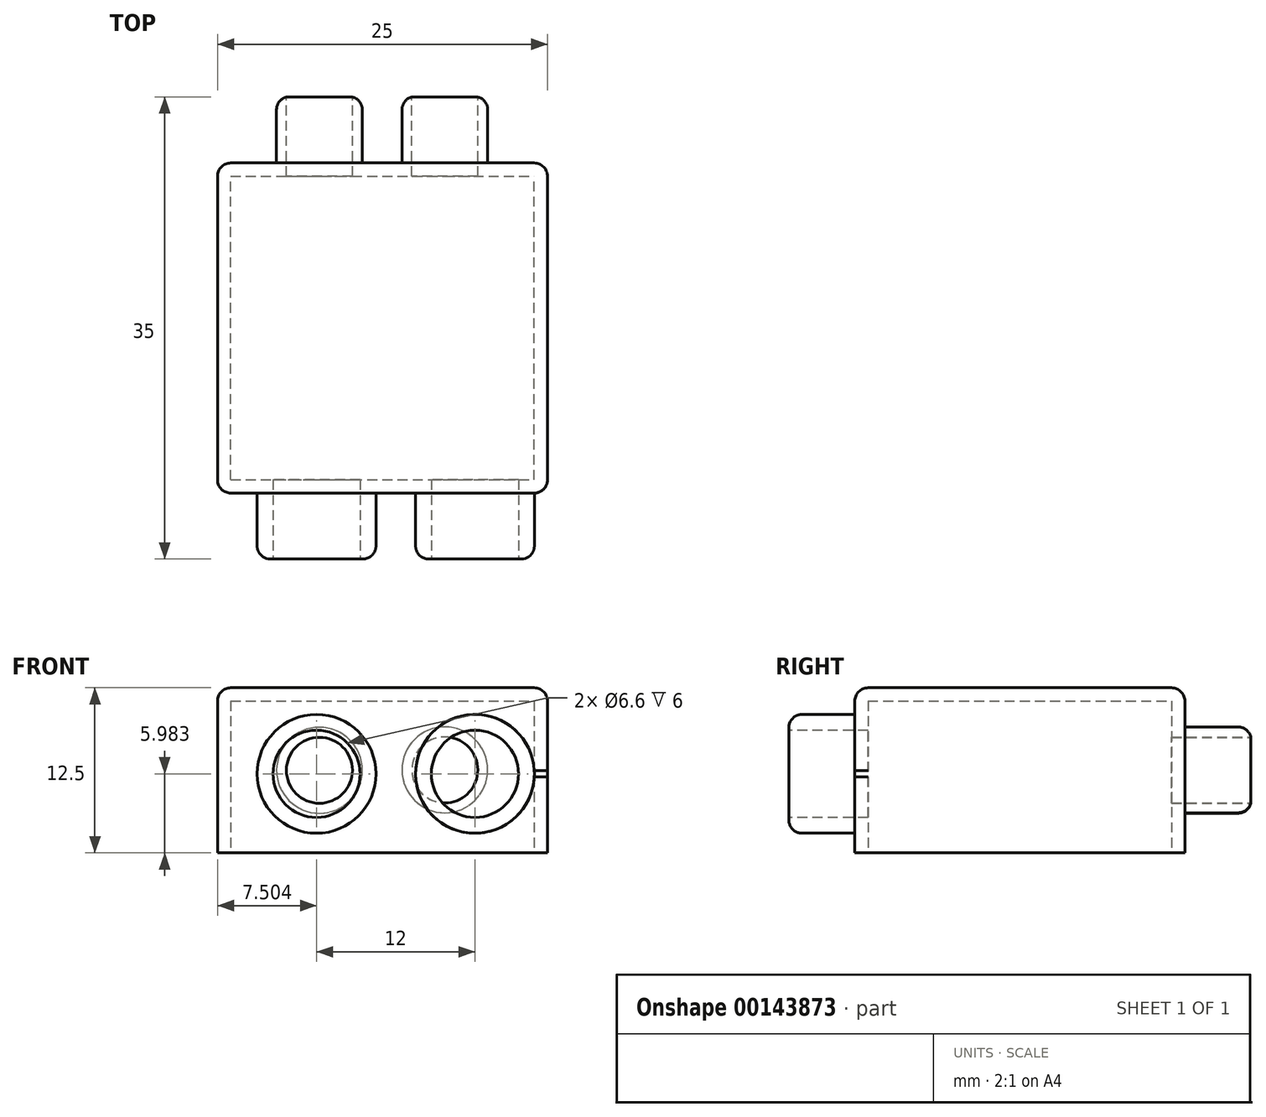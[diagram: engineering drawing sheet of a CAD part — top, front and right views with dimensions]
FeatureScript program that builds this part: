
annotation { "Feature Type Name" : "Feature", "Feature Type Description" : "" }
export const myFeature = defineFeature(function(context is Context, id is Id, definition is map)
    precondition{}
    {
        {
            var Q0;
            Q0=qCreatedBy(makeId("Front.planeOp"),FACE);
            var sketch = newSketch(context, id + "F0", { "sketchPlane" : qUnion([Q0])});
            skCircle(sketch, "E0", {"center": v(-3.06, 9.01) * mm, "radius": 2.5 * mm});
            skCircle(sketch, "E1", {"center": v(6.44, 9.04) * mm, "radius": 2.5 * mm});
            skCircle(sketch, "E2", {"center": v(-3.06, 9.01) * mm, "radius": 3.25 * mm});
            skCircle(sketch, "E3", {"center": v(6.44, 9.04) * mm, "radius": 3.25 * mm});
            skLineSegment(sketch, "E4.bottom", {"start": v(-10.78, 15.26) * mm, "end": v(14.22, 15.26) * mm});
            skLineSegment(sketch, "E4.top", {"start": v(-10.78, 2.76) * mm, "end": v(14.22, 2.76) * mm});
            skLineSegment(sketch, "E4.left", {"start": v(-10.78, 15.26) * mm, "end": v(-10.78, 2.76) * mm});
            skLineSegment(sketch, "E4.right", {"start": v(14.22, 15.26) * mm, "end": v(14.22, 2.76) * mm});
            skSolve(sketch);
        }
        {
            var Q0;
            Q0=makeQuery(id+"F0.imprint","IMPRINT",FACE,{"disambiguationData":[TD([[makeQuery(id+"F0.imprint","IMPRINT",EDGE,{"derivedFrom":sQuery(id+"F0.wireOp",EDGE,"E0")}),-1.0]])]});
            var Q1;
            Q1=makeQuery(id+"F0.imprint","IMPRINT",FACE,{"disambiguationData":[TD([[makeQuery(id+"F0.imprint","IMPRINT",EDGE,{"derivedFrom":sQuery(id+"F0.wireOp",EDGE,"E0")}),1.0]])]});
            var Q2;
            Q2=makeQuery(id+"F0.imprint","IMPRINT",FACE,{"disambiguationData":[TD([[makeQuery(id+"F0.imprint","IMPRINT",EDGE,{"derivedFrom":sQuery(id+"F0.wireOp",EDGE,"E1")}),1.0]])]});
            var Q3;
            Q3=makeQuery(id+"F0.imprint","IMPRINT",FACE,{"disambiguationData":[TD([[makeQuery(id+"F0.imprint","IMPRINT",EDGE,{"derivedFrom":sQuery(id+"F0.wireOp",EDGE,"E1")}),-1.0]])]});
            var Q4;
            Q4=makeQuery(id+"F0.imprint","IMPRINT",FACE,{"disambiguationData":[TD([[makeQuery(id+"F0.imprint","IMPRINT",EDGE,{"derivedFrom":sQuery(id+"F0.wireOp",EDGE,"E2")}),-1.0]])]});
            extrude(context, id + "F1", {"entities" : qUnion([Q0, Q1, Q2, Q3, Q4]), "depth" : 25 * mm});
        }
        {
            var Q0;
            Q0=makeQuery(id+"F1.opExtrude","SWEPT_FACE",FACE,{"disambiguationData":[OSD([sQuery(id+"F0.wireOp",EDGE,"E4.top")])]});
            shell(context, id + "F2", {"entities" : qUnion([Q0]), "thickness" : 1 * mm});
        }
        {
            var Q0;
            Q0=makeQuery(id+"F0.imprint","IMPRINT",FACE,{"disambiguationData":[TD([[makeQuery(id+"F0.imprint","IMPRINT",EDGE,{"derivedFrom":sQuery(id+"F0.wireOp",EDGE,"E1")}),1.0]])]});
            var Q1;
            Q1=makeQuery(id+"F0.imprint","IMPRINT",FACE,{"disambiguationData":[TD([[makeQuery(id+"F0.imprint","IMPRINT",EDGE,{"derivedFrom":sQuery(id+"F0.wireOp",EDGE,"E0")}),1.0]])]});
            extrude(context, id + "F3", {"entities" : qUnion([Q0, Q1]), "operationType" : NewBodyOperationType.REMOVE, "depth" : 10 * mm});
        }
        {
            var Q0;
            Q0=makeQuery(id+"F0.imprint","IMPRINT",FACE,{"disambiguationData":[TD([[makeQuery(id+"F0.imprint","IMPRINT",EDGE,{"derivedFrom":sQuery(id+"F0.wireOp",EDGE,"E0")}),-1.0]])]});
            var Q1;
            Q1=makeQuery(id+"F0.imprint","IMPRINT",FACE,{"disambiguationData":[TD([[makeQuery(id+"F0.imprint","IMPRINT",EDGE,{"derivedFrom":sQuery(id+"F0.wireOp",EDGE,"E1")}),-1.0]])]});
            extrude(context, id + "F4", {"entities" : qUnion([Q0, Q1]), "operationType" : NewBodyOperationType.ADD, "oppositeDirection" : true, "depth" : 5 * mm});
        }
        {
            var Q0;
            Q0=makeQuery(id+"F1.opExtrude","CAP_FACE",FACE,{"disambiguationData":[OSD([sQuery(id+"F0.wireOp",EDGE,"E4.bottom"),sQuery(id+"F0.wireOp",EDGE,"E4.top"),sQuery(id+"F0.wireOp",EDGE,"E4.left"),sQuery(id+"F0.wireOp",EDGE,"E4.right")])],"isStart":false});
            var sketch = newSketch(context, id + "F5", { "sketchPlane" : qUnion([Q0])});
            skCircle(sketch, "E5", {"center": v(-3.28, 8.74) * mm, "radius": 3.3 * mm});
            skCircle(sketch, "E6", {"center": v(-3.28, 8.74) * mm, "radius": 4.5 * mm});
            skCircle(sketch, "E7", {"center": v(8.72, 8.74) * mm, "radius": 3.3 * mm});
            skCircle(sketch, "E8", {"center": v(8.72, 8.74) * mm, "radius": 4.5 * mm});
            skSolve(sketch);
        }
        {
            var Q0;
            Q0=makeQuery(id+"F5.imprint","IMPRINT",FACE,{"disambiguationData":[TD([[makeQuery(id+"F5.imprint","IMPRINT",EDGE,{"derivedFrom":sQuery(id+"F5.wireOp",EDGE,"E5")}),1.0]])]});
            var Q1;
            Q1=makeQuery(id+"F5.imprint","IMPRINT",FACE,{"disambiguationData":[TD([[makeQuery(id+"F5.imprint","IMPRINT",EDGE,{"derivedFrom":sQuery(id+"F5.wireOp",EDGE,"E7")}),1.0]])]});
            extrude(context, id + "F6", {"entities" : qUnion([Q0, Q1]), "operationType" : NewBodyOperationType.REMOVE, "oppositeDirection" : true, "depth" : 10 * mm});
        }
        {
            var Q0;
            Q0=makeQuery(id+"F5.imprint","IMPRINT",FACE,{"disambiguationData":[TD([[makeQuery(id+"F5.imprint","IMPRINT",EDGE,{"derivedFrom":sQuery(id+"F5.wireOp",EDGE,"E5")}),-1.0]])]});
            var Q1;
            Q1=makeQuery(id+"F5.imprint","IMPRINT",FACE,{"disambiguationData":[TD([[makeQuery(id+"F5.imprint","IMPRINT",EDGE,{"derivedFrom":sQuery(id+"F5.wireOp",EDGE,"E7")}),-1.0]])]});
            extrude(context, id + "F7", {"entities" : qUnion([Q0, Q1]), "operationType" : NewBodyOperationType.ADD, "depth" : 5 * mm});
        }
        {
            var Q0;
            Q0=makeQuery(id+"F1.opExtrude","CAP_EDGE",EDGE,{"disambiguationData":[OSD([sQuery(id+"F0.wireOp",EDGE,"E4.right")])],"isStart":false});
            var Q1;
            Q1=makeQuery(id+"F1.opExtrude","SWEPT_EDGE",EDGE,{"disambiguationData":[OSD([sQuery(id+"F0.wireOp",EDGE,"E4.bottom"),sQuery(id+"F0.wireOp",EDGE,"E4.right")])]});
            var Q2;
            Q2=makeQuery(id+"F1.opExtrude","CAP_EDGE",EDGE,{"disambiguationData":[OSD([sQuery(id+"F0.wireOp",EDGE,"E4.bottom")])],"isStart":false});
            var Q3;
            Q3=makeQuery(id+"F1.opExtrude","CAP_EDGE",EDGE,{"disambiguationData":[OSD([sQuery(id+"F0.wireOp",EDGE,"E4.left")])],"isStart":false});
            var Q4;
            Q4=makeQuery(id+"F1.opExtrude","CAP_EDGE",EDGE,{"disambiguationData":[OSD([sQuery(id+"F0.wireOp",EDGE,"E4.right")])],"isStart":true});
            var Q5;
            Q5=makeQuery(id+"F1.opExtrude","CAP_EDGE",EDGE,{"disambiguationData":[OSD([sQuery(id+"F0.wireOp",EDGE,"E4.bottom")])],"isStart":true});
            var Q6;
            Q6=makeQuery(id+"F1.opExtrude","CAP_EDGE",EDGE,{"disambiguationData":[OSD([sQuery(id+"F0.wireOp",EDGE,"E4.left")])],"isStart":true});
            var Q7;
            Q7=makeQuery(id+"F1.opExtrude","SWEPT_EDGE",EDGE,{"disambiguationData":[OSD([sQuery(id+"F0.wireOp",EDGE,"E4.bottom"),sQuery(id+"F0.wireOp",EDGE,"E4.left")])]});
            fillet(context, id + "F8", {"entities" : qUnion([Q0, Q1, Q2, Q3, Q4, Q5, Q6, Q7]), "radius" : 1 * mm, "tangentPropagation" : true, "allowEdgeOverflow" : false});
        }
        {
            var Q0;
            Q0=makeQuery(id+"F4.opExtrude","CAP_EDGE",EDGE,{"disambiguationData":[OSD([sQuery(id+"F0.wireOp",EDGE,"E3")])],"isStart":false});
            var Q1;
            Q1=makeQuery(id+"F4.opExtrude","CAP_EDGE",EDGE,{"disambiguationData":[OSD([sQuery(id+"F0.wireOp",EDGE,"E2")])],"isStart":false});
            var Q2;
            Q2=makeQuery(id+"F7.opExtrude","CAP_EDGE",EDGE,{"disambiguationData":[OSD([sQuery(id+"F5.wireOp",EDGE,"E6")])],"isStart":false});
            var Q3;
            Q3=makeQuery(id+"F7.opExtrude","CAP_EDGE",EDGE,{"disambiguationData":[OSD([sQuery(id+"F5.wireOp",EDGE,"E8")])],"isStart":false});
            fillet(context, id + "F9", {"entities" : qUnion([Q0, Q1, Q2, Q3]), "radius" : 1 * mm, "tangentPropagation" : true, "allowEdgeOverflow" : false});
        }
    });
